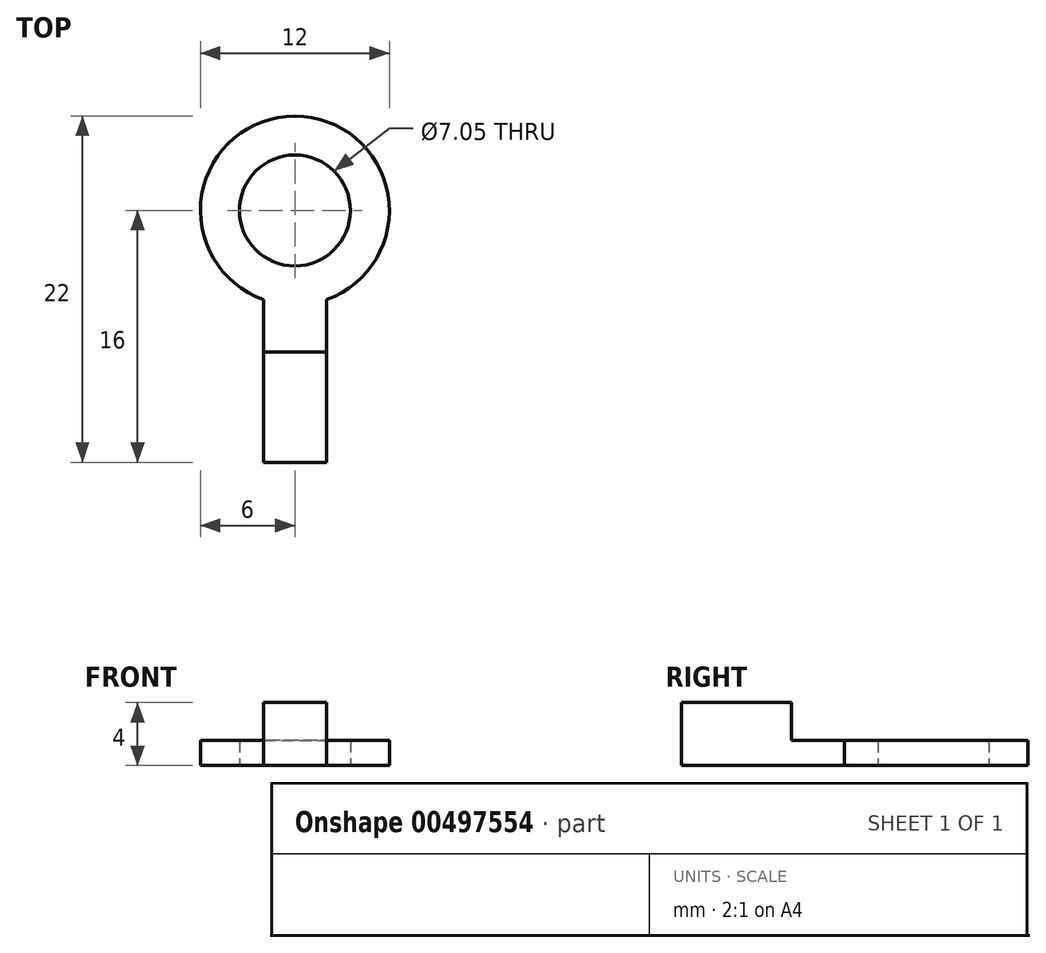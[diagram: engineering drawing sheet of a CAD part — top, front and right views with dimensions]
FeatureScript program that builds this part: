
annotation { "Feature Type Name" : "Feature", "Feature Type Description" : "" }
export const myFeature = defineFeature(function(context is Context, id is Id, definition is map)
    precondition{}
    {
        {
            var Q0;
            Q0=qCreatedBy(makeId("Top.planeOp"),FACE);
            var sketch = newSketch(context, id + "F0", { "sketchPlane" : qUnion([Q0])});
            skLineSegment(sketch, "E0", {"start": v(0, 60) * mm, "end": v(0, -60) * mm});
            skLineSegment(sketch, "E1", {"start": v(-70, 0) * mm, "end": v(70, 0) * mm});
            skCircle(sketch, "E2", {"center": v(0, 0) * mm, "radius": 3.52 * mm});
            skArc(sketch, "E3", {"start": v(2, -5.66) * mm, "mid": v(0, 6) * mm, "end": v(-2, -5.66) * mm});
            skLineSegment(sketch, "E4", {"start": v(2, -5.66) * mm, "end": v(2, -16) * mm});
            skLineSegment(sketch, "E5", {"start": v(-2, -5.66) * mm, "end": v(-2, -16) * mm});
            skLineSegment(sketch, "E6", {"start": v(-2, -9) * mm, "end": v(2, -9) * mm});
            skLineSegment(sketch, "E7", {"start": v(-2, -16) * mm, "end": v(2, -16) * mm});
            skSolve(sketch);
        }
        {
            var Q0;
            {var subQ5=sQuery(id+"F0.wireOp",EDGE,"E2");var subQ7=sQuery(id+"F0.wireOp",EDGE,"E0");var subQ8=makeQuery(id+"F0.imprint","INTERSECT",VERTEX,{"disambiguationData":[OD(1.0)],"derivedFrom":[subQ7,subQ5]});Q0=makeQuery(id+"F0.imprint","IMPRINT",FACE,{"disambiguationData":[TD([[makeQuery(id+"F0.imprint","IMPRINT",EDGE,{"disambiguationData":[TD([[subQ8,-1.0]])],"derivedFrom":subQ7}),-1.0]])]});}
            var Q1;
            {var subQ0=sQuery(id+"F0.wireOp",EDGE,"E2");var subQ1=sQuery(id+"F0.wireOp",EDGE,"E0");var subQ2=makeQuery(id+"F0.imprint","INTERSECT",VERTEX,{"disambiguationData":[OD(1.0)],"derivedFrom":[subQ1,subQ0]});Q1=makeQuery(id+"F0.imprint","IMPRINT",FACE,{"disambiguationData":[TD([[makeQuery(id+"F0.imprint","IMPRINT",EDGE,{"disambiguationData":[TD([[subQ2,-1.0]])],"derivedFrom":subQ1}),1.0]])]});}
            var Q2;
            {var subQ0=sQuery(id+"F0.wireOp",EDGE,"E3");var subQ1=sQuery(id+"F0.wireOp",EDGE,"E0");var subQ2=makeQuery(id+"F0.imprint","INTERSECT",VERTEX,{"derivedFrom":[subQ1,subQ0]});Q2=makeQuery(id+"F0.imprint","IMPRINT",FACE,{"disambiguationData":[TD([[makeQuery(id+"F0.imprint","IMPRINT",EDGE,{"disambiguationData":[TD([[subQ2,-1.0]])],"derivedFrom":subQ1}),1.0]])]});}
            var Q3;
            {var subQ0=sQuery(id+"F0.wireOp",EDGE,"E3");var subQ1=sQuery(id+"F0.wireOp",EDGE,"E0");var subQ2=makeQuery(id+"F0.imprint","INTERSECT",VERTEX,{"derivedFrom":[subQ1,subQ0]});Q3=makeQuery(id+"F0.imprint","IMPRINT",FACE,{"disambiguationData":[TD([[makeQuery(id+"F0.imprint","IMPRINT",EDGE,{"disambiguationData":[TD([[subQ2,-1.0]])],"derivedFrom":subQ1}),-1.0]])]});}
            extrude(context, id + "F1", {"entities" : qUnion([Q0, Q1, Q2, Q3]), "depth" : (6.35 / 4) * mm});
        }
        {
            var Q0;
            Q0=qCreatedBy(makeId("Top.planeOp"),FACE);
            var sketch = newSketch(context, id + "F2", { "sketchPlane" : qUnion([Q0])});
            skLineSegment(sketch, "E8", {"start": v(0, 60) * mm, "end": v(0, -60) * mm});
            skLineSegment(sketch, "E9", {"start": v(-70, 0) * mm, "end": v(70, 0) * mm});
            skCircle(sketch, "E10", {"center": v(0, 0) * mm, "radius": 3.52 * mm});
            skArc(sketch, "E11", {"start": v(2, -5.66) * mm, "mid": v(0, 6) * mm, "end": v(-2, -5.66) * mm});
            skLineSegment(sketch, "E12", {"start": v(2, -5.66) * mm, "end": v(2, -16) * mm});
            skLineSegment(sketch, "E13", {"start": v(-2, -5.66) * mm, "end": v(-2, -16) * mm});
            skLineSegment(sketch, "E14", {"start": v(-2, -9) * mm, "end": v(2, -9) * mm});
            skLineSegment(sketch, "E15", {"start": v(-2, -16) * mm, "end": v(2, -16) * mm});
            skSolve(sketch);
        }
        {
            var Q0;
            {var subQ0=sQuery(id+"F2.wireOp",EDGE,"E15");var subQ1=sQuery(id+"F2.wireOp",EDGE,"E8");var subQ2=makeQuery(id+"F2.imprint","INTERSECT",VERTEX,{"derivedFrom":[subQ1,subQ0]});Q0=makeQuery(id+"F2.imprint","IMPRINT",FACE,{"disambiguationData":[TD([[makeQuery(id+"F2.imprint","IMPRINT",EDGE,{"disambiguationData":[TD([[subQ2,1.0]])],"derivedFrom":subQ1}),-1.0]])]});}
            var Q1;
            {var subQ0=sQuery(id+"F2.wireOp",EDGE,"E15");var subQ1=sQuery(id+"F2.wireOp",EDGE,"E8");var subQ2=makeQuery(id+"F2.imprint","INTERSECT",VERTEX,{"derivedFrom":[subQ1,subQ0]});Q1=makeQuery(id+"F2.imprint","IMPRINT",FACE,{"disambiguationData":[TD([[makeQuery(id+"F2.imprint","IMPRINT",EDGE,{"disambiguationData":[TD([[subQ2,1.0]])],"derivedFrom":subQ1}),1.0]])]});}
            extrude(context, id + "F3", {"entities" : qUnion([Q0, Q1]), "operationType" : NewBodyOperationType.ADD, "depth" : 4 * mm});
        }
    });
